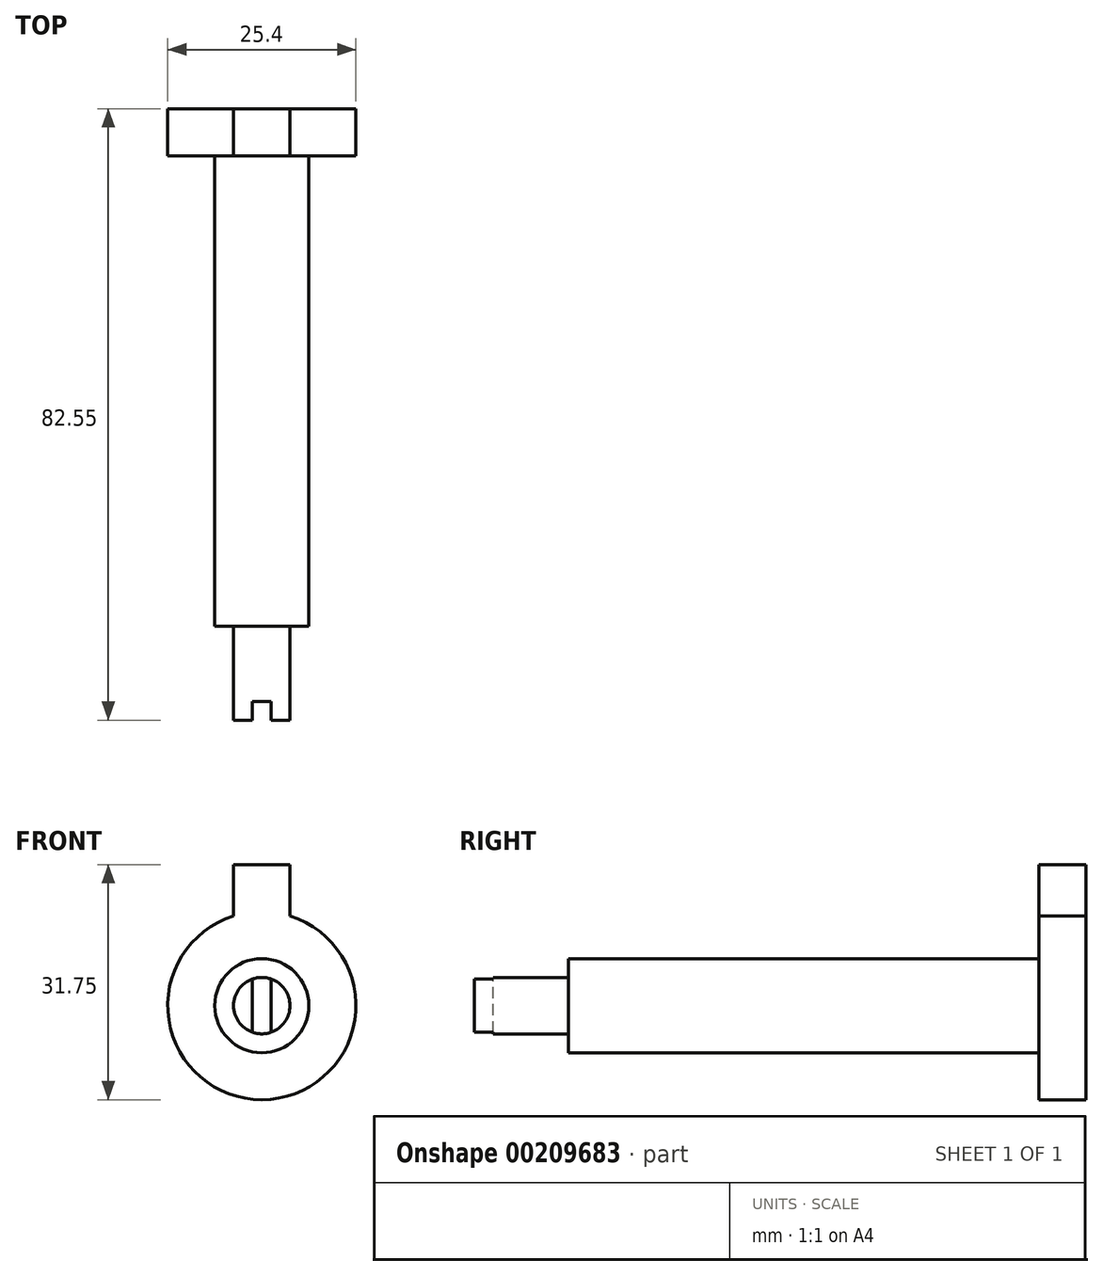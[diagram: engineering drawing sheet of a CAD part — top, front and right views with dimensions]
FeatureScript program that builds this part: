
annotation { "Feature Type Name" : "Feature", "Feature Type Description" : "" }
export const myFeature = defineFeature(function(context is Context, id is Id, definition is map)
    precondition{}
    {
        {
            var Q0;
            Q0=qCreatedBy(makeId("Front.planeOp"),FACE);
            var sketch = newSketch(context, id + "F0", { "sketchPlane" : qUnion([Q0])});
            skArc(sketch, "E0", {"start": v(-3.81, 12.12) * mm, "mid": v(0, -12.7) * mm, "end": v(3.81, 12.12) * mm});
            skLineSegment(sketch, "E1.bottom", {"start": v(3.81, 19.05) * mm, "end": v(-3.8, 19.05) * mm});
            skLineSegment(sketch, "E1.left", {"start": v(3.81, 19.05) * mm, "end": v(3.81, 12.12) * mm});
            skLineSegment(sketch, "E1.right", {"start": v(-3.8, 19.05) * mm, "end": v(-3.8, 12.12) * mm});
            skPoint(sketch, "E1.top.start.orphan", {"position": v(3.8, -19.05) * mm});
            skPoint(sketch, "E2.trimOffspring.end.orphan", {"position": v(-3.8, -19.05) * mm});
            skSolve(sketch);
        }
        {
            var Q0;
            Q0=makeQuery(id+"F0.imprint","IMPRINT",FACE,{"disambiguationData":[TD([[makeQuery(id+"F0.imprint","IMPRINT",EDGE,{"derivedFrom":sQuery(id+"F0.wireOp",EDGE,"E0")}),1.0]])]});
            extrude(context, id + "F1", {"entities" : qUnion([Q0]), "depth" : 6.35 * mm});
        }
        {
            var Q0;
            Q0=makeQuery(id+"F1.opExtrude","CAP_FACE",FACE,{"disambiguationData":[OSD([sQuery(id+"F0.wireOp",EDGE,"E0"),sQuery(id+"F0.wireOp",EDGE,"E1.bottom"),sQuery(id+"F0.wireOp",EDGE,"E1.left"),sQuery(id+"F0.wireOp",EDGE,"E1.right")])],"isStart":false});
            var sketch = newSketch(context, id + "F2", { "sketchPlane" : qUnion([Q0])});
            skCircle(sketch, "E3", {"center": v(0, 0) * mm, "radius": 6.35 * mm});
            skSolve(sketch);
        }
        {
            var Q0;
            Q0 = qSketchRegion(id + "F2", true);
            extrude(context, id + "F3", {"entities" : qUnion([Q0]), "operationType" : NewBodyOperationType.ADD, "depth" : 76.2 * mm});
        }
        {
            var Q0;
            Q0=makeQuery(id+"F3.opExtrude","CAP_FACE",FACE,{"disambiguationData":[OSD([sQuery(id+"F2.wireOp",EDGE,"E3")])],"isStart":false});
            var sketch = newSketch(context, id + "F4", { "sketchPlane" : qUnion([Q0])});
            skCircle(sketch, "E4", {"center": v(0, 0) * mm, "radius": 3.81 * mm});
            skSolve(sketch);
        }
        {
            var Q0;
            Q0=makeQuery(id+"F4.imprint","IMPRINT",FACE,{"disambiguationData":[TD([[makeQuery(id+"F4.imprint","IMPRINT",EDGE,{"derivedFrom":sQuery(id+"F4.wireOp",EDGE,"E4")}),-1.0]])]});
            extrude(context, id + "F5", {"entities" : qUnion([Q0]), "operationType" : NewBodyOperationType.REMOVE, "oppositeDirection" : true, "depth" : 12.7 * mm});
        }
        {
            var Q0;
            Q0=makeQuery(id+"F3.opExtrude","CAP_FACE",FACE,{"disambiguationData":[OSD([sQuery(id+"F2.wireOp",EDGE,"E3")])],"isStart":false});
            var sketch = newSketch(context, id + "F6", { "sketchPlane" : qUnion([Q0])});
            skLineSegment(sketch, "E5.bottom", {"start": v(1.27, -12.7) * mm, "end": v(-1.27, -12.7) * mm});
            skLineSegment(sketch, "E5.top", {"start": v(1.27, 12.7) * mm, "end": v(-1.27, 12.7) * mm});
            skLineSegment(sketch, "E5.left", {"start": v(1.27, -12.7) * mm, "end": v(1.27, 12.7) * mm});
            skLineSegment(sketch, "E5.right", {"start": v(-1.27, -12.7) * mm, "end": v(-1.27, 12.7) * mm});
            skPoint(sketch, "E5.middle", {"position": v(0, 0) * mm});
            skSolve(sketch);
        }
        {
            var Q0;
            Q0 = qSketchRegion(id + "F6", true);
            extrude(context, id + "F7", {"entities" : qUnion([Q0]), "operationType" : NewBodyOperationType.REMOVE, "oppositeDirection" : true, "depth" : 2.54 * mm});
        }
    });
